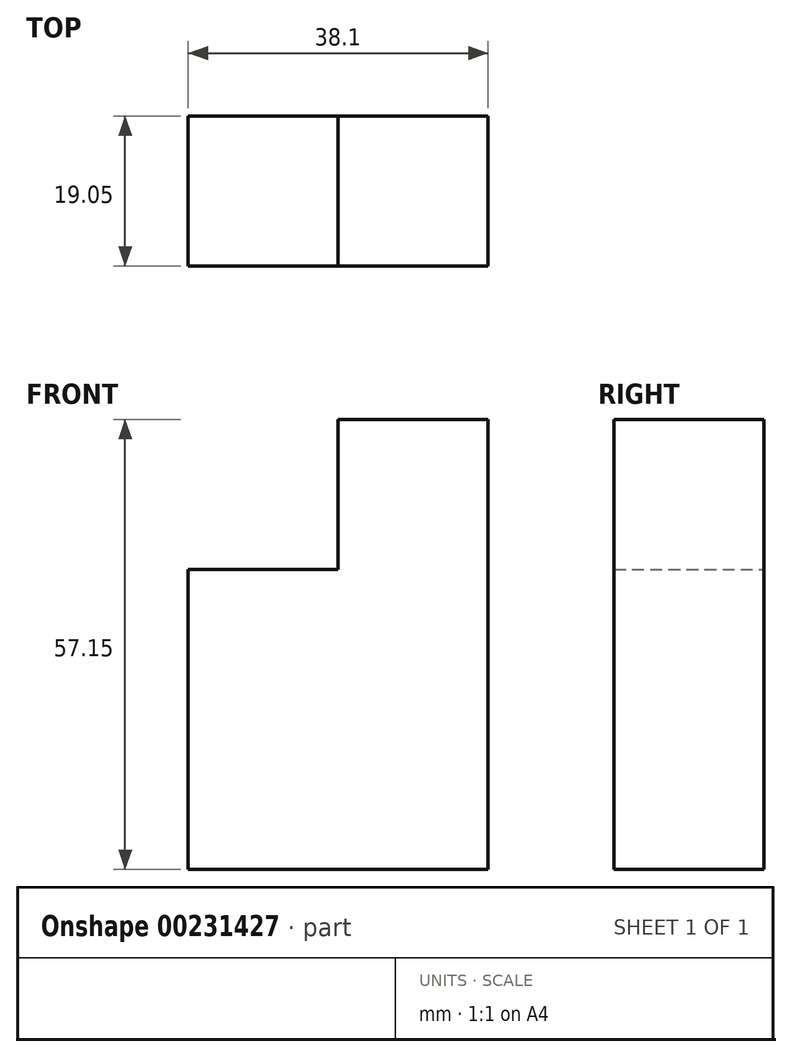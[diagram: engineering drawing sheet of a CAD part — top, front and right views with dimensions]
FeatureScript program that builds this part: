
annotation { "Feature Type Name" : "Feature", "Feature Type Description" : "" }
export const myFeature = defineFeature(function(context is Context, id is Id, definition is map)
    precondition{}
    {
        {
            var Q0;
            Q0=qCreatedBy(makeId("Front.planeOp"),FACE);
            var sketch = newSketch(context, id + "F0", { "sketchPlane" : qUnion([Q0])});
            skLineSegment(sketch, "E0.bottom", {"start": v(-48, 54.11) * mm, "end": v(-28.96, 54.11) * mm});
            skLineSegment(sketch, "E0.top", {"start": v(-48, -3.04) * mm, "end": v(-28.96, -3.04) * mm});
            skLineSegment(sketch, "E0.left", {"start": v(-48, 54.11) * mm, "end": v(-48, -3.04) * mm});
            skLineSegment(sketch, "E0.right", {"start": v(-28.96, 54.11) * mm, "end": v(-28.96, -3.04) * mm});
            skLineSegment(sketch, "E1.bottom", {"start": v(-67.06, 16.01) * mm, "end": v(-48, 16.01) * mm});
            skLineSegment(sketch, "E1.top", {"start": v(-67.06, -3.04) * mm, "end": v(-48, -3.04) * mm});
            skLineSegment(sketch, "E1.left", {"start": v(-67.06, 16.01) * mm, "end": v(-67.06, -3.04) * mm});
            skLineSegment(sketch, "E1.right", {"start": v(-48, 16.01) * mm, "end": v(-48, -3.04) * mm});
            skSolve(sketch);
        }
        {
            var Q0;
            Q0 = qSketchRegion(id + "F0", true);
            extrude(context, id + "F1", {"entities" : qUnion([Q0]), "depth" : 19.05 * mm});
        }
        {
            var Q0;
            Q0=makeQuery(id+"F1.opExtrude","SWEPT_FACE",FACE,{"disambiguationData":[OSD([sQuery(id+"F0.wireOp",EDGE,"E1.bottom")])]});
            var sketch = newSketch(context, id + "F2", { "sketchPlane" : qUnion([Q0])});
            skLineSegment(sketch, "E2.bottom", {"start": v(-48, 0) * mm, "end": v(-67.06, 0) * mm});
            skLineSegment(sketch, "E2.top", {"start": v(-48, -19.05) * mm, "end": v(-67.06, -19.05) * mm});
            skLineSegment(sketch, "E2.left", {"start": v(-48, 0) * mm, "end": v(-48, -19.05) * mm});
            skLineSegment(sketch, "E2.right", {"start": v(-67.06, 0) * mm, "end": v(-67.06, -19.05) * mm});
            skSolve(sketch);
        }
        {
            var Q0;
            Q0 = qSketchRegion(id + "F2", true);
            extrude(context, id + "F3", {"entities" : qUnion([Q0]), "operationType" : NewBodyOperationType.ADD, "depth" : 19.05 * mm});
        }
    });
